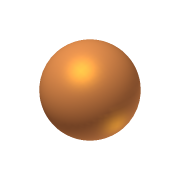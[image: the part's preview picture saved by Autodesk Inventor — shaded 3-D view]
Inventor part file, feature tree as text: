
AUTODESK INVENTOR PART (.ipt)
format: ipt  version: 2012 (Build 160160000, 160)  size: 100,352 bytes
history: native  units: in
note: dims shown in document units (in); Inventor stores cm internally (conversion verified against a paired STEP export)
features: revolve x1, sketch x1
ambient origin geometry x8: Origin, YZ Plane, XZ Plane, XY Plane, X Axis, Y Axis, Z Axis, Center Point
bodies: Solid1 (feature_tree)
feature tree (2):
  revolve  "Revolution1"  Angle=90.0deg
  sketch  "Sketch1"  dims[d0=3.975in d1=90.0deg]
